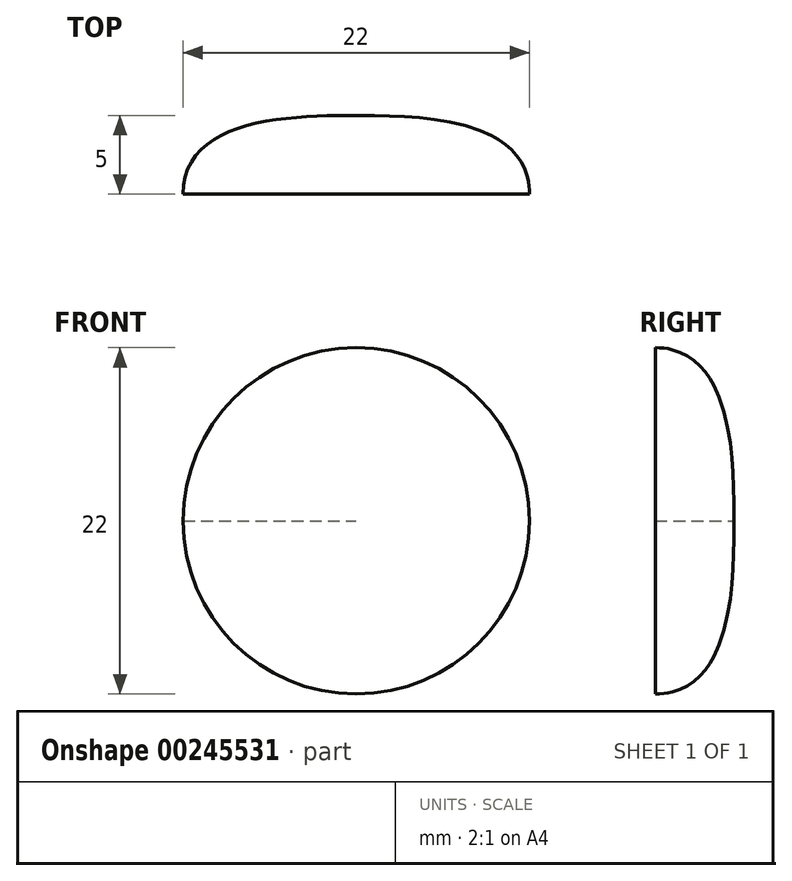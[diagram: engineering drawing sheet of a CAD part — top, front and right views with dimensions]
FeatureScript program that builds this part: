
annotation { "Feature Type Name" : "Feature", "Feature Type Description" : "" }
export const myFeature = defineFeature(function(context is Context, id is Id, definition is map)
    precondition{}
    {
        {
            var Q0;
            Q0=qCreatedBy(makeId("Top.planeOp"),FACE);
            var sketch = newSketch(context, id + "F0", { "sketchPlane" : qUnion([Q0])});
            skLineSegment(sketch, "E0", {"start": v(0, 0) * mm, "end": v(0, 5) * mm});
            skLineSegment(sketch, "E1", {"start": v(0, 0) * mm, "end": v(-11, 0) * mm});
            skFitSpline(sketch, "E2", {"points": [v(-11, 0) * mm, v(-8, 4) * mm, v(0, 5) * mm], "startDerivative": vector(0, 13.62) * mm, "endDerivative": vector(13.4, 0) * mm});
            skSolve(sketch);
        }
        {
            var Q0;
            Q0=makeQuery(id+"F0.imprint","IMPRINT",FACE,{"disambiguationData":[TD([[makeQuery(id+"F0.imprint","IMPRINT",EDGE,{"derivedFrom":sQuery(id+"F0.wireOp",EDGE,"E0")}),1.0]])]});
            var Q1;
            Q1=sQuery(id+"F0.wireOp",EDGE,"E0");
            revolve(context, id + "F1", {"entities" : qUnion([Q0]), "axis" : qUnion([Q1]), "revolveType" : RevolveType.FULL});
        }
    });
